# Revit family: Electronics_Masking-Generators_Biamp_Qt-Patient-Privacy-System_Emitter-W
name_source: partatom
category: Communication Devices
units: mm (PartAtom-declared; Revit-internal decimal feet)

## family parameters
Cut with Voids When Loaded = No
Host = Face
Maintain Annotation Orientation = No
OmniClass Number = 23.85.10.00
OmniClass Title = General Information Systems
Part Type = Normal
Room Calculation Point = No
Round Connector Dimension = Use Diameter
Shared = No

## types (1)
- QT Emitter
    Altitude = 0-6,600 feet (0–2000 Meters) MSL
    Beam Mount = Beam Mount
    Cable Type = UTP Twisted Category 3 Type CMP (Plenum)
    Ceiling Conduit Mount = Ceiling Conduit Mount
    Channel Selection = 4 Channels (Auto Sequencing and Repeating)
    Connector Description = RJ-45 Input
    Default Elevation = 92 "
    Description = QT® Patient Privacy System for Waiting Rooms, Exam Rooms, and Pharmacies
    Driver Diameter = 1.25 inches (32mm)
    Drywall Mount = Drywall Mount
    Drywall Rough-in Mount = Drywall Rough-in Mount
    Grid Material = Biamp - Plastic - White(Grid)
    Housing Material = Biamp - Plastic - White
    Humidity = 0–95%, non-condensing
    Loudspeaker Type = Passive with Transformer
    Manufacturer = Biamp
    Maximum Cabling Distance (per Run) = 1000 feet (300m)
    Maximum Emitter Quantity (per Run) = 60
    Maximum Masking SPL (@ 1m) = 60dBA
    Maximum Music/Paging SPL (@ 1m) = 62dBA
    Maximum Number of Runs = 2
    Minimum Masking SPL (@ 1m) = 30dBA
    Model = QT Emitter
    Music/Paging = 200Hz to 10kHz
    Nominal Dispersion = 170° conical/half space
    Nominal Impedance = 3.6kΩ
    Pendant Mount = Pendant Mount
    Product Documentation Link = https://downloads.biamp.com
    Product Page URL = https://www.biamp.com
    Product data url = https://bimobject.com
    Selectable Attenuation = 0dB, -3dB, -6dB, -9dB
    Sound Masking = 200Hz to 10kHz
    Standard Mount = Standard Mount
    Temperature Range = 40 – 90° F (4 – 32° C)
    URL = https://www.biamp.com
    Universal Mount = Universal Mount
    Version = 1

## geometry (parser evidence)
native form markers: Sweep x22
no freeform markers — native parametric forms only
